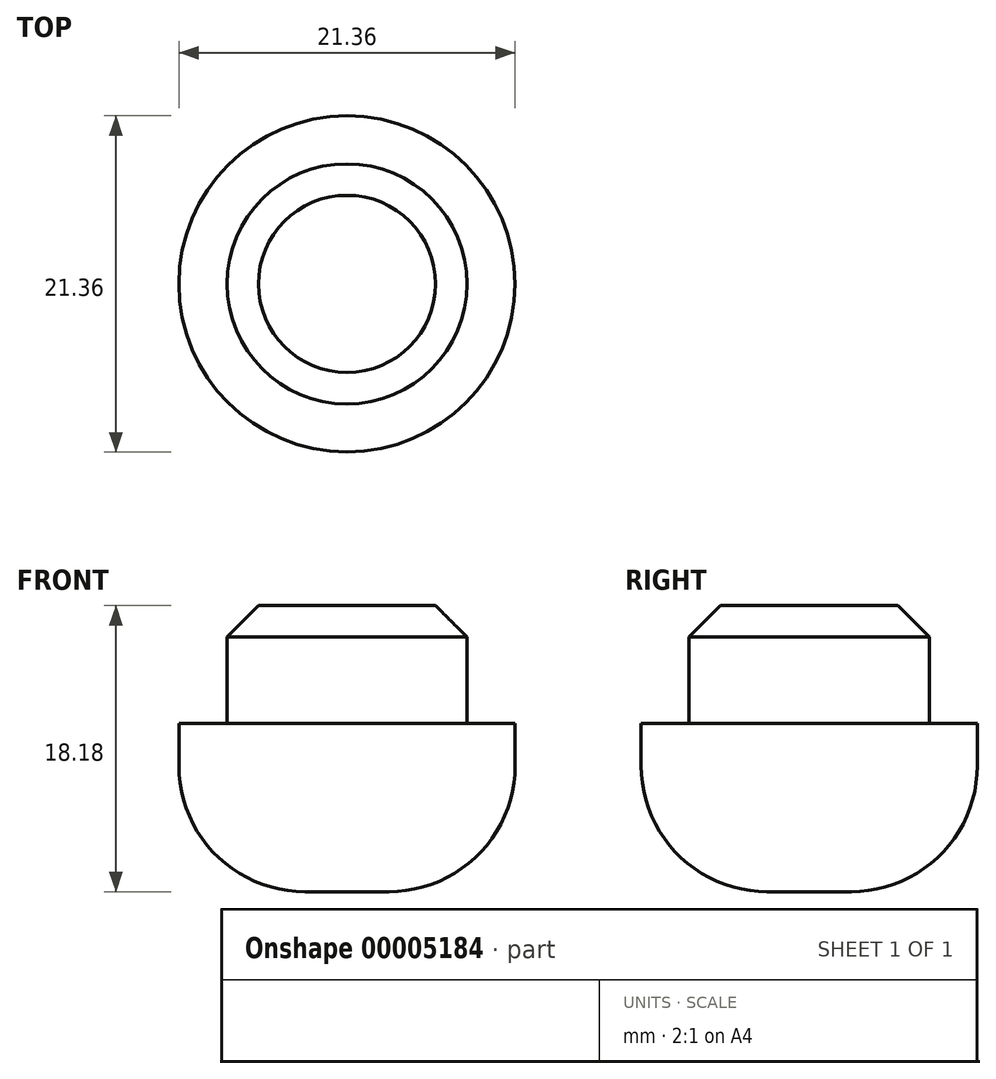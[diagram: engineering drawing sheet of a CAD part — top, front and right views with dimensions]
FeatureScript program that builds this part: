
annotation { "Feature Type Name" : "Feature", "Feature Type Description" : "" }
export const myFeature = defineFeature(function(context is Context, id is Id, definition is map)
    precondition{}
    {
        {
            var Q0;
            Q0=qCreatedBy(makeId("Top.planeOp"),FACE);
            var sketch = newSketch(context, id + "F0", { "sketchPlane" : qUnion([Q0])});
            skCircle(sketch, "E0", {"center": v(0, 0) * mm, "radius": 7.62 * mm});
            skSolve(sketch);
        }
        {
            var Q0;
            Q0 = qSketchRegion(id + "F0", true);
            extrude(context, id + "F1", {"entities" : qUnion([Q0]), "depth" : 7.5 * mm, "offsetDistance" : 25 * mm});
        }
        {
            var Q0;
            Q0=makeQuery(id+"F1.opExtrude","CAP_FACE",FACE,{"disambiguationData":[OSD([sQuery(id+"F0.wireOp",EDGE,"E0")])],"isStart":true});
            var sketch = newSketch(context, id + "F2", { "sketchPlane" : qUnion([Q0])});
            skCircle(sketch, "E1", {"center": v(0, 0) * mm, "radius": 10.68 * mm});
            skSolve(sketch);
        }
        {
            var Q0;
            Q0 = qSketchRegion(id + "F2", true);
            extrude(context, id + "F3", {"entities" : qUnion([Q0]), "operationType" : NewBodyOperationType.ADD, "depth" : (21.35 / 2) * mm, "offsetDistance" : 25 * mm});
        }
        {
            var Q0;
            Q0=makeQuery(id+"F1.opExtrude","CAP_EDGE",EDGE,{"disambiguationData":[OSD([sQuery(id+"F0.wireOp",EDGE,"E0")])],"isStart":false});
            chamfer(context, id + "F4", {"entities" : qUnion([Q0]), "width" : 2 * mm, "tangentPropagation" : true});
        }
        {
            var Q0;
            Q0=makeQuery(id+"F3.opExtrude","CAP_EDGE",EDGE,{"disambiguationData":[OSD([sQuery(id+"F2.wireOp",EDGE,"E1")])],"isStart":false});
            fillet(context, id + "F5", {"entities" : qUnion([Q0]), "radius" : 8 * mm, "tangentPropagation" : true, "allowEdgeOverflow" : false});
        }
    });
